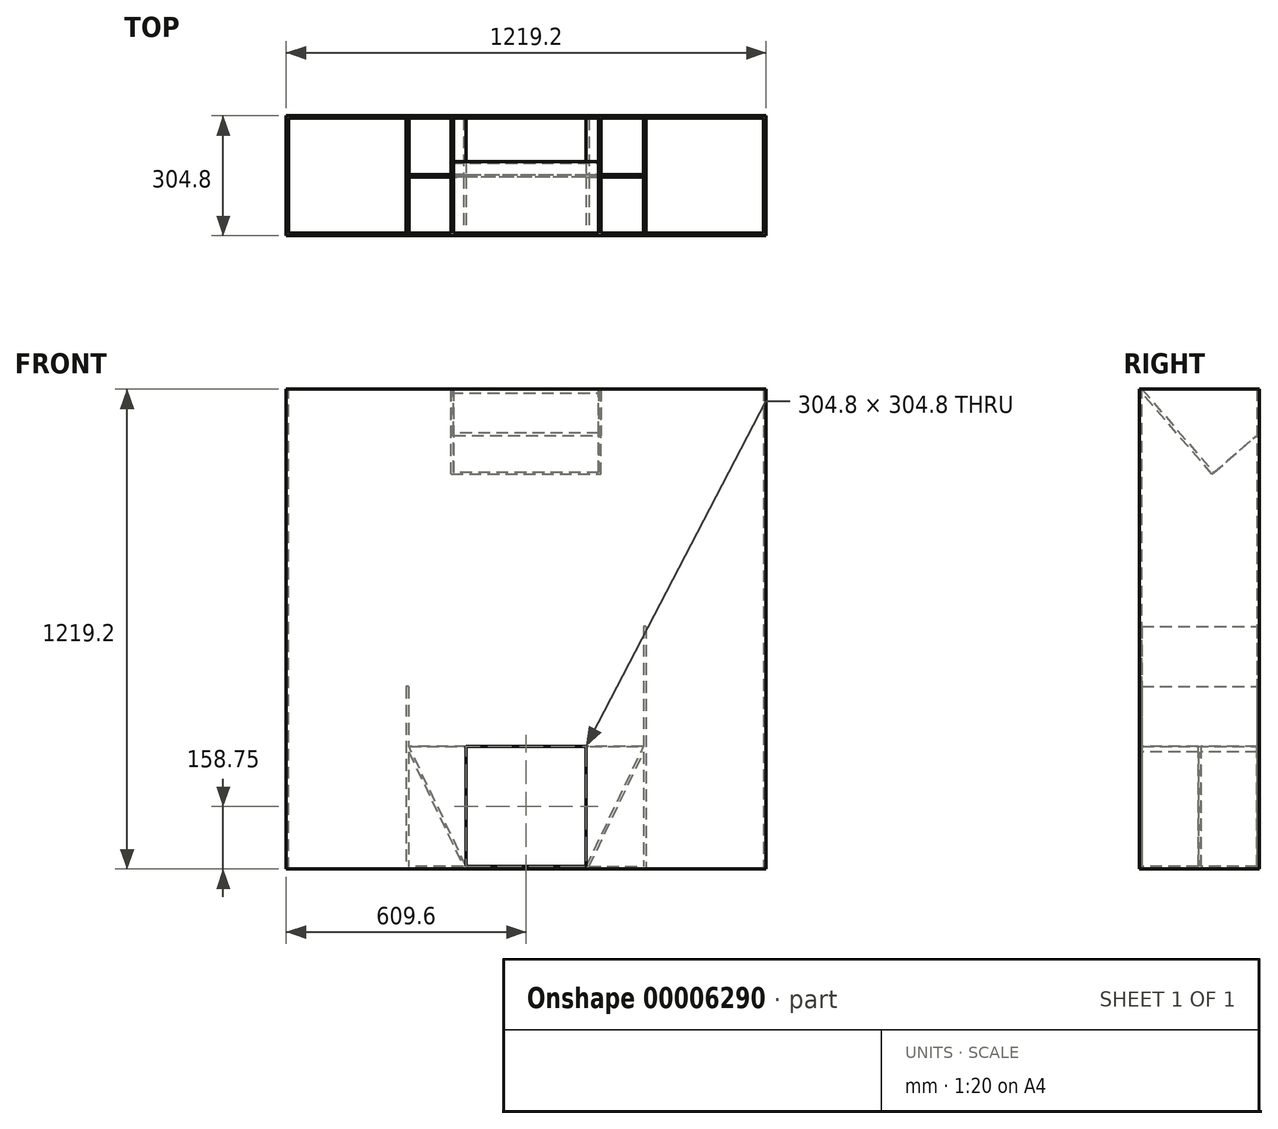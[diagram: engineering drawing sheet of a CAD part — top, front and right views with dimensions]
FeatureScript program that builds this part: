
annotation { "Feature Type Name" : "Feature", "Feature Type Description" : "" }
export const myFeature = defineFeature(function(context is Context, id is Id, definition is map)
    precondition{}
    {
        {
            var Q0;
            Q0=qCreatedBy(makeId("Front.planeOp"),FACE);
            var sketch = newSketch(context, id + "F0", { "sketchPlane" : qUnion([Q0])});
            skLineSegment(sketch, "E0", {"start": v(0, 0) * mm, "end": v(0, 1219.2) * mm});
            skLineSegment(sketch, "E1", {"start": v(0, 1219.2) * mm, "end": v(1219.2, 1219.2) * mm});
            skLineSegment(sketch, "E2", {"start": v(1219.2, 1219.2) * mm, "end": v(1219.2, 0) * mm});
            skLineSegment(sketch, "E3", {"start": v(1219.2, 0) * mm, "end": v(0, 0) * mm});
            skSolve(sketch);
        }
        {
            var Q0;
            Q0=makeQuery(id+"F0.imprint","IMPRINT",FACE,{"disambiguationData":[TD([[makeQuery(id+"F0.imprint","IMPRINT",EDGE,{"derivedFrom":sQuery(id+"F0.wireOp",EDGE,"E0")}),-1.0]])]});
            extrude(context, id + "F1", {"entities" : qUnion([Q0]), "depth" : 304.8 * mm});
        }
        {
            var Q0;
            Q0=sQuery(id+"F0.wireOp",EDGE,"E3");
            cPlane(context, id + "F2", {"entities" : qUnion([Q0]), "cplaneType" : CPlaneType.MID_PLANE, "offset" : 152.4 * mm, "width" : 152.4 * mm, "height" : 152.4 * mm});
        }
        {
            var Q0;
            Q0=makeQuery(id+"F1.opExtrude","SWEPT_FACE",FACE,{"disambiguationData":[OSD([sQuery(id+"F0.wireOp",EDGE,"E1")])]});
            shell(context, id + "F3", {"entities" : qUnion([Q0]), "thickness" : 6.35 * mm});
        }
        {
            var Q0;
            Q0=makeQuery(id+"F1.opExtrude","SWEPT_FACE",FACE,{"disambiguationData":[OSD([sQuery(id+"F0.wireOp",EDGE,"E3")])]});
            var sketch = newSketch(context, id + "F4", { "sketchPlane" : qUnion([Q0])});
            skLineSegment(sketch, "E4.0", {"start": v(0, 304.8) * mm, "end": v(0, 0) * mm});
            skLineSegment(sketch, "E4.1", {"start": v(1219.2, 304.8) * mm, "end": v(0, 304.8) * mm});
            skLineSegment(sketch, "E4.2", {"start": v(1219.2, 304.8) * mm, "end": v(1219.2, 0) * mm});
            skLineSegment(sketch, "E4.3", {"start": v(1219.2, 0) * mm, "end": v(0, 0) * mm});
            skLineSegment(sketch, "E5", {"start": v(0, 152.4) * mm, "end": v(1219.2, 152.4) * mm, "construction": true});
            skLineSegment(sketch, "E6", {"start": v(304.8, 298.45) * mm, "end": v(304.8, 6.35) * mm});
            skLineSegment(sketch, "E7", {"start": v(311.15, 298.45) * mm, "end": v(311.15, 6.35) * mm});
            skLineSegment(sketch, "E8", {"start": v(311.15, 149.22) * mm, "end": v(609.6, 149.22) * mm});
            skLineSegment(sketch, "E9", {"start": v(609.6, 155.57) * mm, "end": v(311.15, 155.57) * mm});
            skLineSegment(sketch, "E10.0", {"start": v(6.35, 298.45) * mm, "end": v(6.35, 6.35) * mm});
            skLineSegment(sketch, "E11", {"start": v(609.6, 304.8) * mm, "end": v(609.6, 0) * mm, "construction": true});
            skLineSegment(sketch, "E12", {"start": v(609.6, 155.57) * mm, "end": v(609.6, 149.22) * mm});
            skLineSegment(sketch, "E13.0.MirrorCS", {"start": v(609.6, 155.57) * mm, "end": v(908.05, 155.58) * mm});
            skLineSegment(sketch, "E14.0.MirrorCS", {"start": v(908.05, 149.22) * mm, "end": v(609.6, 149.22) * mm});
            skLineSegment(sketch, "E15.0.MirrorCS", {"start": v(908.05, 298.45) * mm, "end": v(908.05, 6.35) * mm});
            skLineSegment(sketch, "E16.0.MirrorCS", {"start": v(914.4, 298.45) * mm, "end": v(914.4, 6.35) * mm});
            skLineSegment(sketch, "E17.0.MirrorCS", {"start": v(1212.85, 298.45) * mm, "end": v(1212.85, 6.35) * mm});
            skLineSegment(sketch, "E18.0", {"start": v(1212.85, 298.45) * mm, "end": v(908.05, 298.45) * mm});
            skLineSegment(sketch, "E19.trimOffspring", {"start": v(311.15, 298.45) * mm, "end": v(6.35, 298.45) * mm});
            skLineSegment(sketch, "E20.0", {"start": v(1212.85, 6.35) * mm, "end": v(908.05, 6.35) * mm});
            skLineSegment(sketch, "E21.trimOffspring", {"start": v(311.15, 6.35) * mm, "end": v(6.35, 6.35) * mm});
            skSolve(sketch);
        }
        {
            var Q0;
            {var subQ2=sQuery(id+"F4.wireOp",EDGE,"E6");Q0=makeQuery(id+"F4.imprint","IMPRINT",FACE,{"disambiguationData":[TD([[makeQuery(id+"F4.imprint","IMPRINT",EDGE,{"derivedFrom":subQ2}),-1.0]])]});}
            var Q1;
            {var subQ2=sQuery(id+"F4.wireOp",EDGE,"E16.0.MirrorCS");Q1=makeQuery(id+"F4.imprint","IMPRINT",FACE,{"disambiguationData":[TD([[makeQuery(id+"F4.imprint","IMPRINT",EDGE,{"derivedFrom":subQ2}),1.0]])]});}
            var Q2;
            Q2=makeQuery(id+"F3.opShell","OFFSET_FACE",FACE,{"disambiguationData":[OSD([sQuery(id+"F0.wireOp",EDGE,"E3")])]});
            extrude(context, id + "F5", {"entities" : qUnion([Q0, Q1]), "operationType" : NewBodyOperationType.REMOVE, "endBound" : BoundingType.UP_TO_SURFACE, "oppositeDirection" : true, "endBoundEntityFace" : qUnion([Q2]), "depth" : 25.4 * mm});
        }
        {
            var Q0;
            Q0=makeQuery(id+"F1.opExtrude","CAP_FACE",FACE,{"disambiguationData":[OSD([sQuery(id+"F0.wireOp",EDGE,"E0"),sQuery(id+"F0.wireOp",EDGE,"E1"),sQuery(id+"F0.wireOp",EDGE,"E2"),sQuery(id+"F0.wireOp",EDGE,"E3")])],"isStart":false});
            var sketch = newSketch(context, id + "F6", { "sketchPlane" : qUnion([Q0])});
            skLineSegment(sketch, "E22", {"start": v(762, 6.35) * mm, "end": v(762, 311.15) * mm});
            skLineSegment(sketch, "E23", {"start": v(914.4, 311.15) * mm, "end": v(609.6, 311.15) * mm});
            skLineSegment(sketch, "E24", {"start": v(609.6, 6.35) * mm, "end": v(609.6, 311.15) * mm, "construction": true});
            skLineSegment(sketch, "E25.0", {"start": v(1212.85, 6.35) * mm, "end": v(6.35, 6.35) * mm});
            skLineSegment(sketch, "E26", {"start": v(914.4, 311.15) * mm, "end": v(914.4, 0) * mm});
            skLineSegment(sketch, "E27", {"start": v(762, 6.35) * mm, "end": v(907.36, 311.15) * mm});
            skLineSegment(sketch, "E28", {"start": v(914.4, 311.15) * mm, "end": v(769.04, 6.35) * mm});
            skLineSegment(sketch, "E29.0.MirrorCS", {"start": v(304.8, 311.15) * mm, "end": v(609.6, 311.15) * mm});
            skLineSegment(sketch, "E30.0.MirrorCS", {"start": v(457.2, 6.35) * mm, "end": v(457.2, 311.15) * mm});
            skLineSegment(sketch, "E31.0.MirrorCS", {"start": v(457.2, 6.35) * mm, "end": v(311.84, 311.15) * mm});
            skLineSegment(sketch, "E32.0.MirrorCS", {"start": v(304.8, 311.15) * mm, "end": v(450.16, 6.35) * mm});
            skLineSegment(sketch, "E33.0.MirrorCS", {"start": v(304.8, 311.15) * mm, "end": v(304.8, 0) * mm});
            skSolve(sketch);
        }
        {
            var Q0;
            {var subQ1=sQuery(id+"F6.wireOp",EDGE,"E22");Q0=makeQuery(id+"F6.imprint","IMPRINT",FACE,{"disambiguationData":[TD([[makeQuery(id+"F6.imprint","IMPRINT",EDGE,{"derivedFrom":subQ1}),1.0]])]});}
            extrude(context, id + "F7", {"entities" : qUnion([Q0]), "operationType" : NewBodyOperationType.REMOVE, "endBound" : BoundingType.THROUGH_ALL, "oppositeDirection" : true, "depth" : 25.4 * mm});
        }
        {
            var Q0;
            Q0=qCreatedBy(id+"F2.planeOp",FACE);
            var sketch = newSketch(context, id + "F8", { "sketchPlane" : qUnion([Q0])});
            skLineSegment(sketch, "E34.0", {"start": v(298.45, 62.9) * mm, "end": v(298.45, 1219.2) * mm});
            skLineSegment(sketch, "E35", {"start": v(298.45, 1219.2) * mm, "end": v(115.84, 1007.73) * mm});
            skLineSegment(sketch, "E36", {"start": v(120.65, 1003.58) * mm, "end": v(298.45, 1209.48) * mm});
            skLineSegment(sketch, "E37", {"start": v(120.65, 1003.58) * mm, "end": v(0, 1107.76) * mm});
            skLineSegment(sketch, "E38.0", {"start": v(304.8, 1219.2) * mm, "end": v(0, 1219.2) * mm});
            skLineSegment(sketch, "E39.0", {"start": v(0, 0) * mm, "end": v(0, 1225.55) * mm});
            skLineSegment(sketch, "E39.1", {"start": v(304.8, 0) * mm, "end": v(304.8, 1225.55) * mm});
            skLineSegment(sketch, "E40", {"start": v(0, 1225.55) * mm, "end": v(304.8, 1225.55) * mm});
            skSolve(sketch);
        }
        {
            var Q0;
            {var subQ2=sQuery(id+"F8.wireOp",EDGE,"E35");Q0=makeQuery(id+"F8.imprint","IMPRINT",FACE,{"disambiguationData":[TD([[makeQuery(id+"F8.imprint","IMPRINT",EDGE,{"derivedFrom":subQ2}),1.0]])]});}
            var Q1;
            {var subQ5=sQuery(id+"F8.wireOp",EDGE,"E35");Q1=makeQuery(id+"F8.imprint","IMPRINT",FACE,{"disambiguationData":[TD([[makeQuery(id+"F8.imprint","IMPRINT",EDGE,{"derivedFrom":subQ5}),-1.0]])]});}
            extrude(context, id + "F9", {"entities" : qUnion([Q0, Q1]), "operationType" : NewBodyOperationType.ADD, "endBound" : BoundingType.SYMMETRIC, "depth" : 381 * mm});
        }
        {
            var Q0;
            {var subQ5=sQuery(id+"F8.wireOp",EDGE,"E35");Q0=makeQuery(id+"F8.imprint","IMPRINT",FACE,{"disambiguationData":[TD([[makeQuery(id+"F8.imprint","IMPRINT",EDGE,{"derivedFrom":subQ5}),-1.0]])]});}
            extrude(context, id + "F10", {"entities" : qUnion([Q0]), "operationType" : NewBodyOperationType.REMOVE, "endBound" : BoundingType.SYMMETRIC, "oppositeDirection" : true, "depth" : 368.3 * mm});
        }
        {
            var Q0;
            {var subQ1=sQuery(id+"F4.wireOp",EDGE,"0833d60c-477b-4f6b-a3d2-cdfeb502d10e");Q0=makeQuery(id+"F4.imprint","IMPRINT",FACE,{"disambiguationData":[TD([[makeQuery(id+"F4.imprint","IMPRINT",EDGE,{"derivedFrom":subQ1}),-1.0]])]});}
            var Q1;
            {var subQ0=sQuery(id+"F4.wireOp",EDGE,"E16.0.MirrorCS");Q1=makeQuery(id+"F4.imprint","IMPRINT",FACE,{"disambiguationData":[TD([[makeQuery(id+"F4.imprint","IMPRINT",EDGE,{"derivedFrom":subQ0}),-1.0]])]});}
            extrude(context, id + "F11", {"entities" : qUnion([Q0, Q1]), "operationType" : NewBodyOperationType.ADD, "oppositeDirection" : true, "depth" : 615.95 * mm});
        }
        {
            var Q0;
            {var subQ3=sQuery(id+"F4.wireOp",EDGE,"E6");Q0=makeQuery(id+"F4.imprint","IMPRINT",FACE,{"disambiguationData":[TD([[makeQuery(id+"F4.imprint","IMPRINT",EDGE,{"derivedFrom":subQ3}),1.0]])]});}
            extrude(context, id + "F12", {"entities" : qUnion([Q0]), "operationType" : NewBodyOperationType.ADD, "oppositeDirection" : true, "depth" : 463.55 * mm});
        }
        {
            var Q0;
            {var subQ1=sQuery(id+"F4.wireOp",EDGE,"E8");Q0=makeQuery(id+"F4.imprint","IMPRINT",FACE,{"disambiguationData":[TD([[makeQuery(id+"F4.imprint","IMPRINT",EDGE,{"derivedFrom":subQ1}),1.0]])]});}
            var Q1;
            Q1=makeQuery(id+"F4.imprint","IMPRINT",FACE,{"disambiguationData":[TD([[makeQuery(id+"F4.imprint","IMPRINT",EDGE,{"derivedFrom":sQuery(id+"F4.wireOp",EDGE,"E12")}),1.0]])]});
            extrude(context, id + "F13", {"entities" : qUnion([Q0, Q1]), "operationType" : NewBodyOperationType.ADD, "oppositeDirection" : true, "depth" : 311.15 * mm});
        }
        {
            var Q0;
            {var subQ1=sQuery(id+"F6.wireOp",EDGE,"E27");Q0=makeQuery(id+"F6.imprint","IMPRINT",FACE,{"disambiguationData":[TD([[makeQuery(id+"F6.imprint","IMPRINT",EDGE,{"derivedFrom":subQ1}),-1.0]])]});}
            var Q1;
            {var subQ1=sQuery(id+"F6.wireOp",EDGE,"E31.0.MirrorCS");Q1=makeQuery(id+"F6.imprint","IMPRINT",FACE,{"disambiguationData":[TD([[makeQuery(id+"F6.imprint","IMPRINT",EDGE,{"derivedFrom":subQ1}),1.0]])]});}
            extrude(context, id + "F14", {"entities" : qUnion([Q0, Q1]), "operationType" : NewBodyOperationType.ADD, "oppositeDirection" : true, "depth" : 304.8 * mm});
        }
    });
